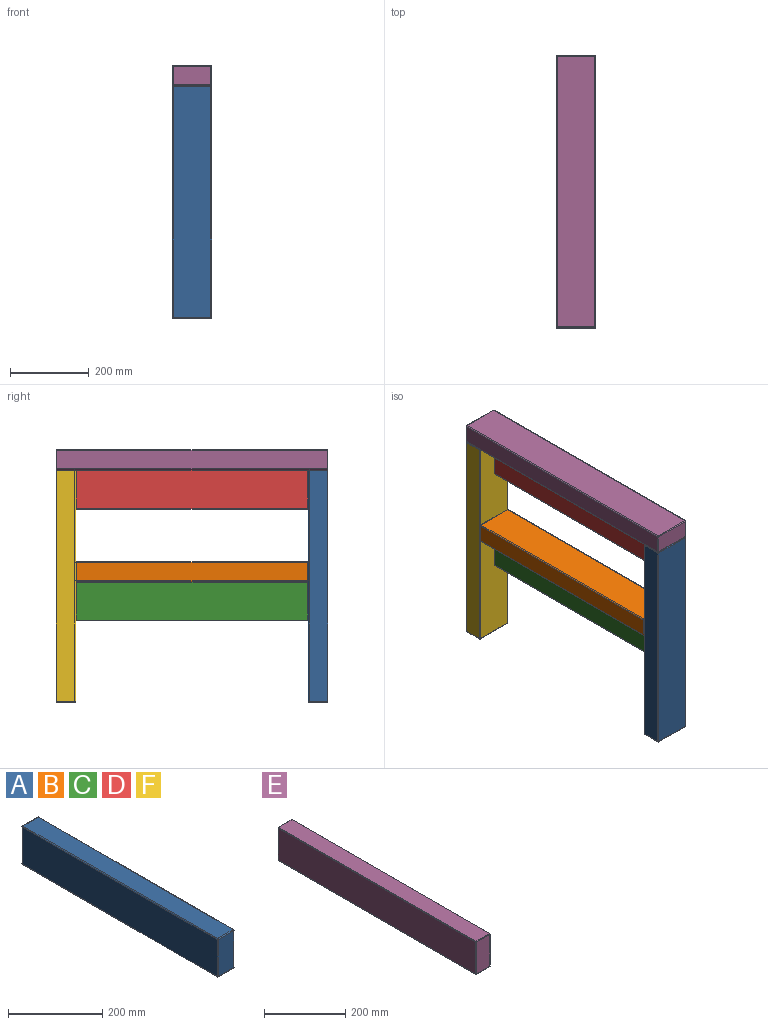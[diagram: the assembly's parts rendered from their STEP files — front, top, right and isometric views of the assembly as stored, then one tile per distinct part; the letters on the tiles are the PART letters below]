
ASSEMBLY  parts=6 mates=15
PART A: 26 faces, bbox 50x590x100 mm
  f0: plane 586x46mm, normal (0,0,-1), area 26956mm2, adj f14,f19,f22,f25
  f1: plane 586x96mm, normal (1,0,0), area 56256mm2, adj f11,f20,f21,f25
  f2: plane 586x46mm, normal (0,0,1), area 26956mm2, adj f6,f10,f11,f12
  f3: plane 586x96mm, normal (-1,0,0), area 56256mm2, adj f6,f9,f13,f14
  f4: plane 96x46mm, normal (0,-1,0), area 4416mm2, adj f9,f10,f19,f20
  f5: plane 96x46mm, normal (0,1,0), area 4416mm2, adj f12,f13,f21,f22
  f6: cylinder r=2mm len=586mm, axis (0,1,0), area 1841mm2, adj f2,f3,f7,f8
  f7: sphere r=2mm, area 6.3mm2, adj f6,f9,f10
  f8: sphere r=2mm, area 6.3mm2, adj f6,f12,f13
  f9: cylinder r=2mm len=96mm, axis (0,0,1), area 301.6mm2, adj f3,f4,f7,f15
  f10: cylinder r=2mm len=46mm, axis (1,0,0), area 144.5mm2, adj f2,f4,f7,f16
  f11: cylinder r=2mm len=586mm, axis (0,-1,0), area 1841mm2, adj f1,f2,f16,f17
  f12: cylinder r=2mm len=46mm, axis (-1,0,0), area 144.5mm2, adj f2,f5,f8,f17
  f13: cylinder r=2mm len=96mm, axis (0,0,-1), area 301.6mm2, adj f3,f5,f8,f18
  f14: cylinder r=2mm len=586mm, axis (0,-1,0), area 1841mm2, adj f0,f3,f15,f18
  f15: sphere r=2mm, area 6.3mm2, adj f9,f14,f19
  f16: sphere r=2mm, area 6.3mm2, adj f10,f11,f20
  f17: sphere r=2mm, area 6.3mm2, adj f11,f12,f21
  f18: sphere r=2mm, area 6.3mm2, adj f13,f14,f22
  f19: cylinder r=2mm len=46mm, axis (-1,0,0), area 144.5mm2, adj f0,f4,f15,f23
  f20: cylinder r=2mm len=96mm, axis (0,0,-1), area 301.6mm2, adj f1,f4,f16,f23
  f21: cylinder r=2mm len=96mm, axis (0,0,1), area 301.6mm2, adj f1,f5,f17,f24
  f22: cylinder r=2mm len=46mm, axis (1,0,0), area 144.5mm2, adj f0,f5,f18,f24
  f23: sphere r=2mm, area 6.3mm2, adj f19,f20,f25
  f24: sphere r=2mm, area 6.3mm2, adj f21,f22,f25
  f25: cylinder r=2mm len=586mm, axis (0,1,0), area 1841mm2, adj f0,f1,f23,f24
PART B: same geometry as A
PART C: same geometry as A
PART D: same geometry as A
PART E: 26 faces, bbox 50x690x100 mm
  f0: plane 686x46mm, normal (0,0,-1), area 31556mm2, adj f14,f19,f22,f25
  f1: plane 686x96mm, normal (1,0,0), area 65856mm2, adj f11,f20,f21,f25
  f2: plane 686x46mm, normal (0,0,1), area 31556mm2, adj f6,f10,f11,f12
  f3: plane 686x96mm, normal (-1,0,0), area 65856mm2, adj f6,f9,f13,f14
  f4: plane 96x46mm, normal (0,-1,0), area 4416mm2, adj f9,f10,f19,f20
  f5: plane 96x46mm, normal (0,1,0), area 4416mm2, adj f12,f13,f21,f22
  f6: cylinder r=2mm len=686mm, axis (0,1,0), area 2155.1mm2, adj f2,f3,f7,f8
  f7: sphere r=2mm, area 6.3mm2, adj f6,f9,f10
  f8: sphere r=2mm, area 6.3mm2, adj f6,f12,f13
  f9: cylinder r=2mm len=96mm, axis (0,0,1), area 301.6mm2, adj f3,f4,f7,f15
  f10: cylinder r=2mm len=46mm, axis (1,0,0), area 144.5mm2, adj f2,f4,f7,f16
  f11: cylinder r=2mm len=686mm, axis (0,-1,0), area 2155.1mm2, adj f1,f2,f16,f17
  f12: cylinder r=2mm len=46mm, axis (-1,0,0), area 144.5mm2, adj f2,f5,f8,f17
  f13: cylinder r=2mm len=96mm, axis (0,0,-1), area 301.6mm2, adj f3,f5,f8,f18
  f14: cylinder r=2mm len=686mm, axis (0,-1,0), area 2155.1mm2, adj f0,f3,f15,f18
  f15: sphere r=2mm, area 6.3mm2, adj f9,f14,f19
  f16: sphere r=2mm, area 6.3mm2, adj f10,f11,f20
  f17: sphere r=2mm, area 6.3mm2, adj f11,f12,f21
  f18: sphere r=2mm, area 6.3mm2, adj f13,f14,f22
  f19: cylinder r=2mm len=46mm, axis (-1,0,0), area 144.5mm2, adj f0,f4,f15,f23
  f20: cylinder r=2mm len=96mm, axis (0,0,-1), area 301.6mm2, adj f1,f4,f16,f23
  f21: cylinder r=2mm len=96mm, axis (0,0,1), area 301.6mm2, adj f1,f5,f17,f24
  f22: cylinder r=2mm len=46mm, axis (1,0,0), area 144.5mm2, adj f0,f5,f18,f24
  f23: sphere r=2mm, area 6.3mm2, adj f19,f20,f25
  f24: sphere r=2mm, area 6.3mm2, adj f21,f22,f25
  f25: cylinder r=2mm len=686mm, axis (0,1,0), area 2155.1mm2, adj f0,f1,f23,f24
PART F: same geometry as A
PLACE A rot(axis=(-0.58,0.58,-0.58),120deg) t=(-48.26,-361.95,-373.28)mm fixed
PLACE B rot(axis=(-0.71,0,0.71),180deg) t=(-48.26,-41.95,-337.28)mm
PLACE C t=(-23.26,-41.95,-412.28)mm
PLACE D t=(-23.26,-41.95,-128.28)mm
PLACE E rot(axis=(0,-1,0),90deg) t=(-48.26,-41.95,-53.28)mm
PLACE F rot(axis=(-0.58,-0.58,0.58),120deg) t=(-48.26,278.05,-373.28)mm
MATE planar F.f4 <-> E.f3  axis (0,0,1) through (-48.26,278.05,-78.28)mm
MATE planar B.f0 <-> F.f0  axis (1,0,0) through (1.74,-41.95,-337.28)mm
MATE planar C.f2 <-> B.f1  axis (0,0,1) through (-23.26,-41.95,-362.28)mm
MATE planar E.f0 <-> A.f2  axis (1,0,0) through (1.74,-41.95,-53.28)mm
MATE planar B.f5 <-> A.f3  axis (0,-1,0) through (-48.26,-336.95,-337.28)mm
MATE planar D.f4 <-> A.f3  axis (0,-1,0) through (-23.26,-336.95,-128.28)mm
MATE planar C.f4 <-> A.f3  axis (0,-1,0) through (-23.26,-336.95,-412.28)mm
MATE planar F.f1 <-> E.f5  axis (0,1,0) through (-48.26,303.05,-373.28)mm
MATE planar B.f0 <-> A.f2  axis (1,0,0) through (1.74,-41.95,-337.28)mm
MATE planar E.f3 <-> A.f4  axis (0,0,-1) through (-48.26,-41.95,-78.28)mm
MATE planar B.f3 <-> A.f11  axis (0,0,1) through (-48.26,-41.95,-312.28)mm
MATE planar C.f1 <-> B.f0  axis (1,0,0) through (1.74,-41.95,-412.28)mm
MATE planar A.f1 <-> E.f4  axis (0,-1,0) through (-48.26,-386.95,-373.28)mm
MATE planar D.f1 <-> A.f2  axis (1,0,0) through (1.74,-41.95,-176.28)mm
MATE planar D.f2 <-> E.f12  axis (0,0,1) through (-23.26,-41.95,-78.28)mm
